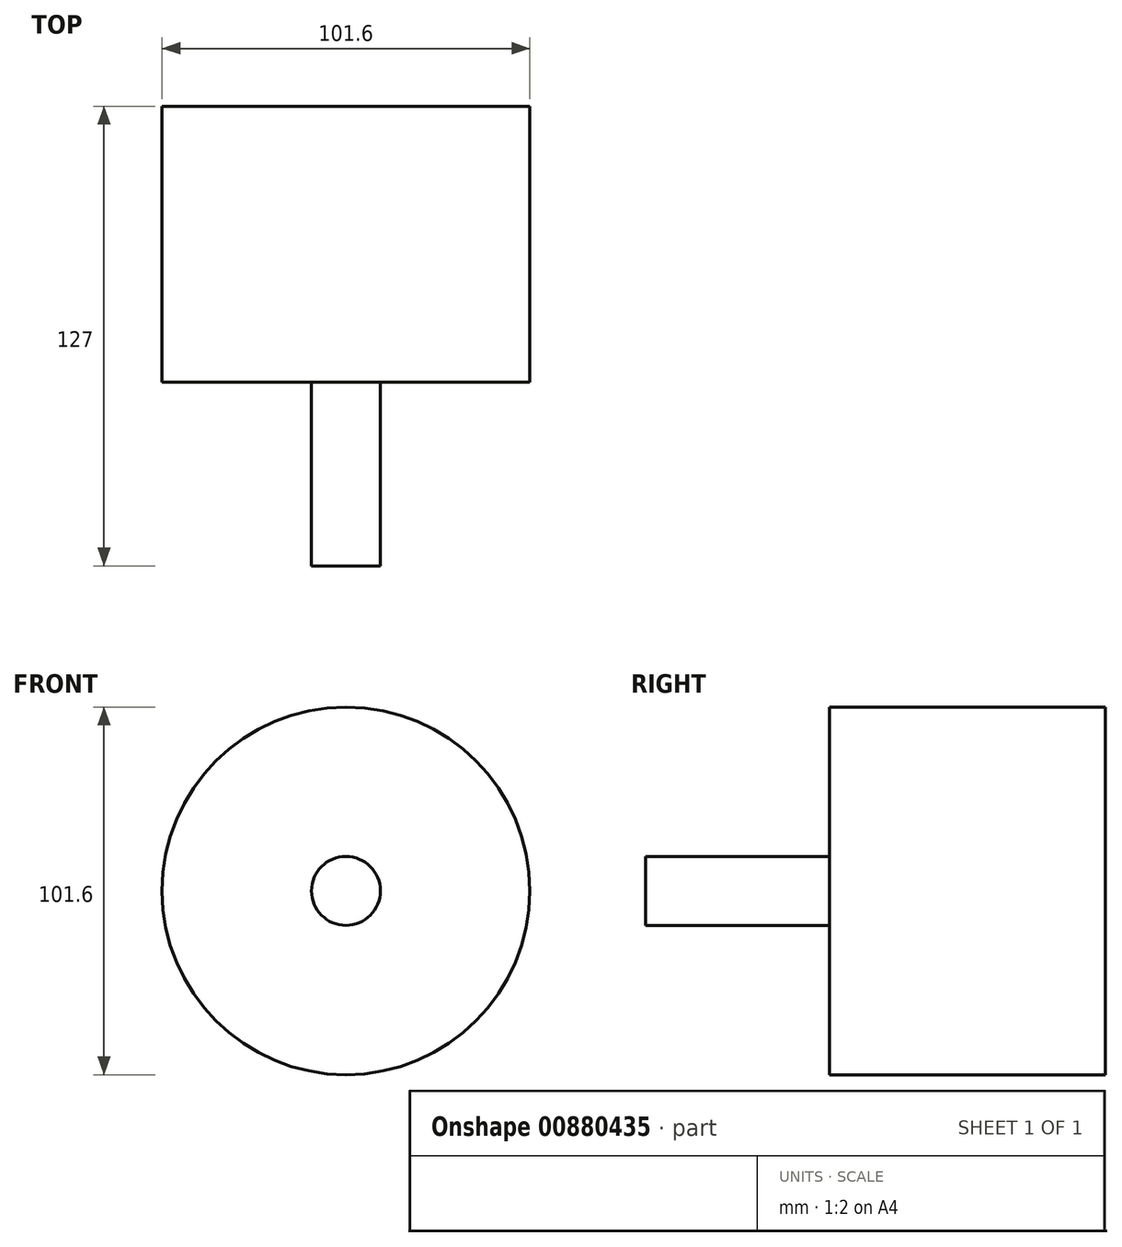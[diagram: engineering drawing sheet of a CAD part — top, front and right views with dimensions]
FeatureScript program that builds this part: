
annotation { "Feature Type Name" : "Feature", "Feature Type Description" : "" }
export const myFeature = defineFeature(function(context is Context, id is Id, definition is map)
    precondition{}
    {
        {
            var Q0;
            Q0=qCreatedBy(makeId("Front.planeOp"),FACE);
            var sketch = newSketch(context, id + "F0", { "sketchPlane" : qUnion([Q0])});
            skCircle(sketch, "E0", {"center": v(0, 0) * mm, "radius": 50.8 * mm});
            skCircle(sketch, "E1", {"center": v(0, 0) * mm, "radius": 9.53 * mm});
            skSolve(sketch);
        }
        {
            var Q0;
            Q0 = qSketchRegion(id + "F0", true);
            var Q1;
            Q1=makeQuery(id+"F0.imprint","IMPRINT",FACE,{"disambiguationData":[TD([[makeQuery(id+"F0.imprint","IMPRINT",EDGE,{"derivedFrom":sQuery(id+"F0.wireOp",EDGE,"E1")}),1.0]])]});
            extrude(context, id + "F1", {"entities" : qUnion([Q0, Q1]), "oppositeDirection" : true, "depth" : 76.2 * mm, "offsetDistance" : 25.4 * mm});
        }
        {
            var Q0;
            Q0=makeQuery(id+"F0.imprint","IMPRINT",FACE,{"disambiguationData":[TD([[makeQuery(id+"F0.imprint","IMPRINT",EDGE,{"derivedFrom":sQuery(id+"F0.wireOp",EDGE,"E1")}),1.0]])]});
            extrude(context, id + "F2", {"entities" : qUnion([Q0]), "operationType" : NewBodyOperationType.ADD, "depth" : 50.8 * mm, "offsetDistance" : 25.4 * mm});
        }
    });
